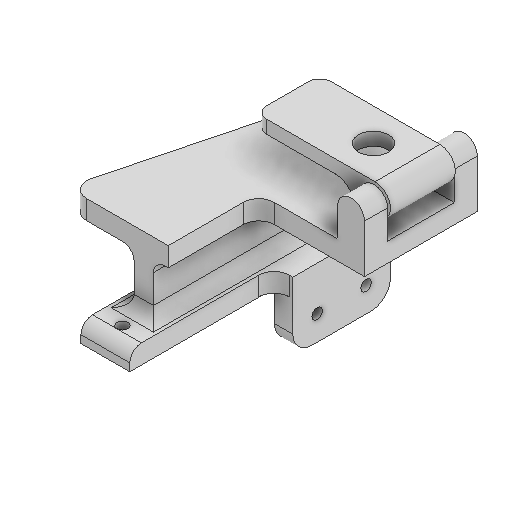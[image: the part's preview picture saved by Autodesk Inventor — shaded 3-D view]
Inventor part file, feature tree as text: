
AUTODESK INVENTOR PART (.ipt)
format: ipt  version: 2025 (Build 290162000, 162)  size: 579,584 bytes
history: native  units: mm
features: sketch x20, extrude x19, projected_geometry x18, fillet x7, plane x6, mirror x2, helix x1
ambient origin geometry x8: Origin, YZ Plane, XZ Plane, XY Plane, X Axis, Y Axis, Z Axis, Center Point
bodies: Solid1 (feature_tree)
feature tree (73):
  extrude  "Extrusion1"  Depth=152.4mm
  plane  "Work Plane1"
  extrude  "Extrusion2"  [1 undecoded]
  extrude  "Extrusion3"  Depth=0.25mm
  extrude  "Extrusion4"  Depth=25.4mm
  fillet  "Fillet1"  Radius=2.75mm
  extrude  "Extrusion5"  Depth=10.0mm TaperAngle=0.0deg
  extrude  "Extrusion6"  Depth=10.0mm
  extrude  "Extrusion7"  Depth=10.0mm TaperAngle=0.0deg
  extrude  "Extrusion8"  Depth=10.0mm TaperAngle=0.0deg
  extrude  "Extrusion9"  Depth=25.4mm TaperAngle=0.0deg
  extrude  "Extrusion10"  Depth=14.0mm
  extrude  "Extrusion11"  Depth=8.0mm
  plane  "Work Plane2"
  extrude  "Extrusion12"  Depth=15.0mm
  mirror  "Mirror1"
  plane  "Work Plane3"
  sketch  "Sketch13"  dims[d37=0.5mm d38=0.5mm]
  plane  "Work Plane4"
  extrude  "Extrusion13"  Depth=0.5mm
  extrude  "Extrusion14"  Depth=10.0mm
  fillet  "Fillet2"  Radius=55.0mm
  fillet  "Fillet3"  [1 undecoded]
  fillet  "Fillet4"  Radius=10.0mm
  extrude  "Extrusion15"  Depth=6.0mm
  extrude  "Extrusion16"  TaperAngle=0.0deg  [1 undecoded]
  fillet  "Fillet5"  Radius=1.5mm
  extrude  "Extrusion17"  Depth=6.0mm
  extrude  "Extrusion18"  Depth=6.0mm TaperAngle=0.0deg
  fillet  "Fillet6"  Radius=6.0mm
  fillet  "Fillet7"  Radius=6.0mm
  plane  "Work Plane5"
  helix  "Coil2"  [1 undecoded]
  plane  "Work Plane6"
  extrude  "Extrusion19"  Depth=10.0mm
  mirror  "Mirror2"
  sketch  "Sketch1"  dims[d0=25.4mm d1=152.4mm]
  sketch  "Sketch2"  dims[d2=10.0mm d3=0.0mm d4=-50.8mm]
  projected_geometry  "Projected Loop1"
  sketch  "Sketch3"  dims[d5=25.4mm d6=0.25mm]
  projected_geometry  "Projected Loop2"
  sketch  "Sketch4"  dims[d7=50.8mm d8=0.0mm d9=25.4mm d10=2.75mm]
  sketch  "Sketch5"  dims[d11=35.45mm d12=0.0mm d13=10.0mm d14=0.0mm]
  projected_geometry  "Projected Loop3"
  sketch  "Sketch6"  dims[d15=10.0mm d16=55.0mm]
  projected_geometry  "Projected Loop4"
  sketch  "Sketch7"  dims[d17=55.0mm d18=10.0mm d19=0.0mm]
  projected_geometry  "Projected Loop5"
  sketch  "Sketch8"  dims[d20=0.0mm d21=0.0mm d22=10.0mm d23=0.0mm]
  projected_geometry  "Projected Loop6"
  sketch  "Sketch9"  dims[d24=25.4mm d25=0.0mm d26=25.4mm d27=0.0mm]
  projected_geometry  "Projected Loop7"
  sketch  "Sketch10"  dims[d28=55.0mm d29=0.0mm d30=14.0mm]
  projected_geometry  "Projected Loop8"
  sketch  "Sketch11"  dims[d31=12.0mm d32=0.0mm d33=8.0mm]
  projected_geometry  "Projected Loop9"
  sketch  "Sketch12"  dims[d34=12.0mm d35=0.0mm d36=15.0mm]
  projected_geometry  "Projected Loop10"
  projected_geometry  "Projected Loop11"
  sketch  "Sketch14"  dims[d39=16.0mm d40=0.5mm d41=55.0mm d42=0.0mm d43=0.0mm d44=0.0mm d45=10.0mm]
  projected_geometry  "Projected Loop12"
  sketch  "Sketch15"  dims[d46=8.0mm d47=6.0mm]
  projected_geometry  "Projected Loop13"
  sketch  "Sketch16"  dims[d48=12.7mm d49=0.0mm d50=0.0mm d53=1.5mm]
  sketch  "Sketch17"  dims[d54=15.0mm d55=0.0mm d56=6.0mm]
  projected_geometry  "Projected Loop14"
  sketch  "Sketch18"  dims[d57=20.0mm d58=0.0mm d59=20.0mm d60=0.0mm d61=6.0mm d62=6.0mm d71=2.0mm]
  projected_geometry  "Projected Loop15"
  sketch  "Sketch19"  dims[d72=3.0mm d73=10.0mm d74=50.0mm d75=0.0mm d76=90.0deg d77=90.0deg d78=0.0mm d79=0.0mm d80=6.35mm d81=61.0mm]
  projected_geometry  "Projected Loop16"
  sketch  "Sketch20"  dims[d82=2.5mm d83=2.5mm d84=0.0mm d85=0.0mm]
  projected_geometry  "Projected Loop17"
  projected_geometry  "Projected Loop18"
note: 4 required parameter values undecoded (feature->parameter linkage not recoverable at this tier; creation-order binding heuristic only, values carry confidence <= 0.55)
